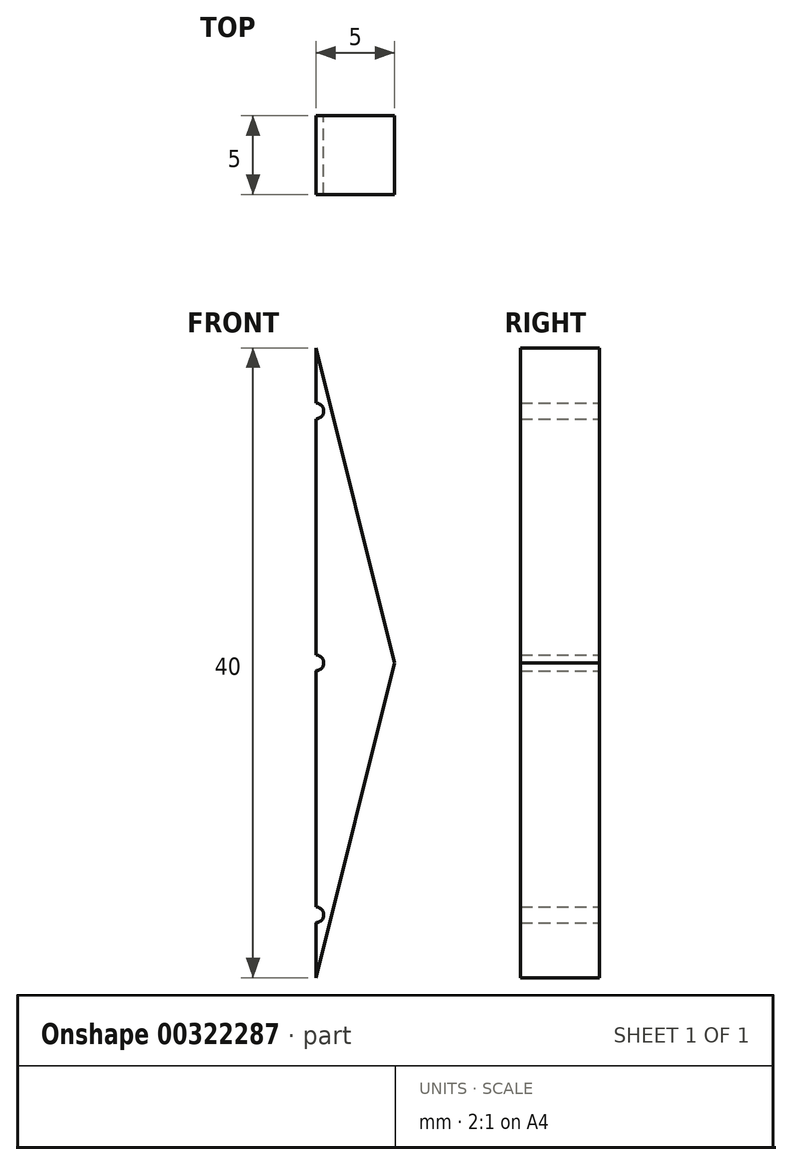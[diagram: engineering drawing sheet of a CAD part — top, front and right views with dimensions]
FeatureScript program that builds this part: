
annotation { "Feature Type Name" : "Feature", "Feature Type Description" : "" }
export const myFeature = defineFeature(function(context is Context, id is Id, definition is map)
    precondition{}
    {
        {
            var Q0;
            Q0=qCreatedBy(makeId("Front.planeOp"),FACE);
            var sketch = newSketch(context, id + "F0", { "sketchPlane" : qUnion([Q0])});
            skLineSegment(sketch, "E0", {"start": v(0, 0) * mm, "end": v(0, 40) * mm});
            skPoint(sketch, "E1", {"position": v(0, 20) * mm});
            skLineSegment(sketch, "E2", {"start": v(0, 20) * mm, "end": v(-5, 20) * mm});
            skLineSegment(sketch, "E3", {"start": v(-5, 20) * mm, "end": v(5, 20) * mm});
            skLineSegment(sketch, "E4", {"start": v(5, 20) * mm, "end": v(0, 20) * mm});
            skLineSegment(sketch, "E5", {"start": v(0, 40) * mm, "end": v(-5, 20) * mm});
            skLineSegment(sketch, "E6", {"start": v(-5, 20) * mm, "end": v(0, 0) * mm});
            skLineSegment(sketch, "E7", {"start": v(5, 20) * mm, "end": v(0, 0) * mm});
            skLineSegment(sketch, "E8", {"start": v(5, 20) * mm, "end": v(0, 40) * mm});
            skPoint(sketch, "E9", {"position": v(0, 36) * mm});
            skPoint(sketch, "E10", {"position": v(0, 4) * mm});
            skSolve(sketch);
        }
        {
            var Q0;
            {var subQ2=sQuery(id+"F0.wireOp",EDGE,"E3");Q0=makeQuery(id+"F0.imprint","IMPRINT",FACE,{"disambiguationData":[TD([[makeQuery(id+"F0.imprint","IMPRINT",EDGE,{"derivedFrom":subQ2}),-1.0]])]});}
            var Q1;
            {var subQ2=sQuery(id+"F0.wireOp",EDGE,"E4");Q1=makeQuery(id+"F0.imprint","IMPRINT",FACE,{"disambiguationData":[TD([[makeQuery(id+"F0.imprint","IMPRINT",EDGE,{"derivedFrom":subQ2}),1.0]])]});}
            var Q2;
            {var subQ2=sQuery(id+"F0.wireOp",EDGE,"E4");Q2=makeQuery(id+"F0.imprint","IMPRINT",FACE,{"disambiguationData":[TD([[makeQuery(id+"F0.imprint","IMPRINT",EDGE,{"derivedFrom":subQ2}),-1.0]])]});}
            var Q3;
            {var subQ2=sQuery(id+"F0.wireOp",EDGE,"E3");Q3=makeQuery(id+"F0.imprint","IMPRINT",FACE,{"disambiguationData":[TD([[makeQuery(id+"F0.imprint","IMPRINT",EDGE,{"derivedFrom":subQ2}),1.0]])]});}
            extrude(context, id + "F1", {"entities" : qUnion([Q0, Q1, Q2, Q3]), "depth" : 5 * mm});
        }
        {
            var Q0;
            Q0=sQuery(id+"F0.wireOp",VERTEX,"E1");
            var Q1;
            Q1=makeQuery(id+"F1.opExtrude","SWEPT_BODY",BODY,{"disambiguationData":[OSD([sQuery(id+"F0.wireOp",EDGE,"E5"),sQuery(id+"F0.wireOp",EDGE,"E6"),sQuery(id+"F0.wireOp",EDGE,"E7"),sQuery(id+"F0.wireOp",EDGE,"E8")])]});
            hole(context, id + "F2", {"style" : HoleStyle.SIMPLE, "endStyle" : HoleEndStyle.THROUGH, "oppositeDirection" : true, "holeDiameter" : 1 * mm, "isTappedThrough" : true, "tappedDepth" : 12 * mm, "tapClearance" : 3, "locations" : qUnion([Q0]), "scope" : qUnion([Q1])});
        }
        {
            var Q0;
            Q0=sQuery(id+"F0.wireOp",VERTEX,"E10");
            var Q1;
            Q1=sQuery(id+"F0.wireOp",VERTEX,"E9");
            var Q2;
            Q2=makeQuery(id+"F1.opExtrude","SWEPT_BODY",BODY,{"disambiguationData":[OSD([sQuery(id+"F0.wireOp",EDGE,"E5"),sQuery(id+"F0.wireOp",EDGE,"E6"),sQuery(id+"F0.wireOp",EDGE,"E7"),sQuery(id+"F0.wireOp",EDGE,"E8")])]});
            hole(context, id + "F3", {"style" : HoleStyle.SIMPLE, "endStyle" : HoleEndStyle.THROUGH, "oppositeDirection" : true, "holeDiameter" : 1 * mm, "isTappedThrough" : true, "tappedDepth" : 12 * mm, "tapClearance" : 3, "locations" : qUnion([Q0, Q1]), "scope" : qUnion([Q2])});
        }
    });
